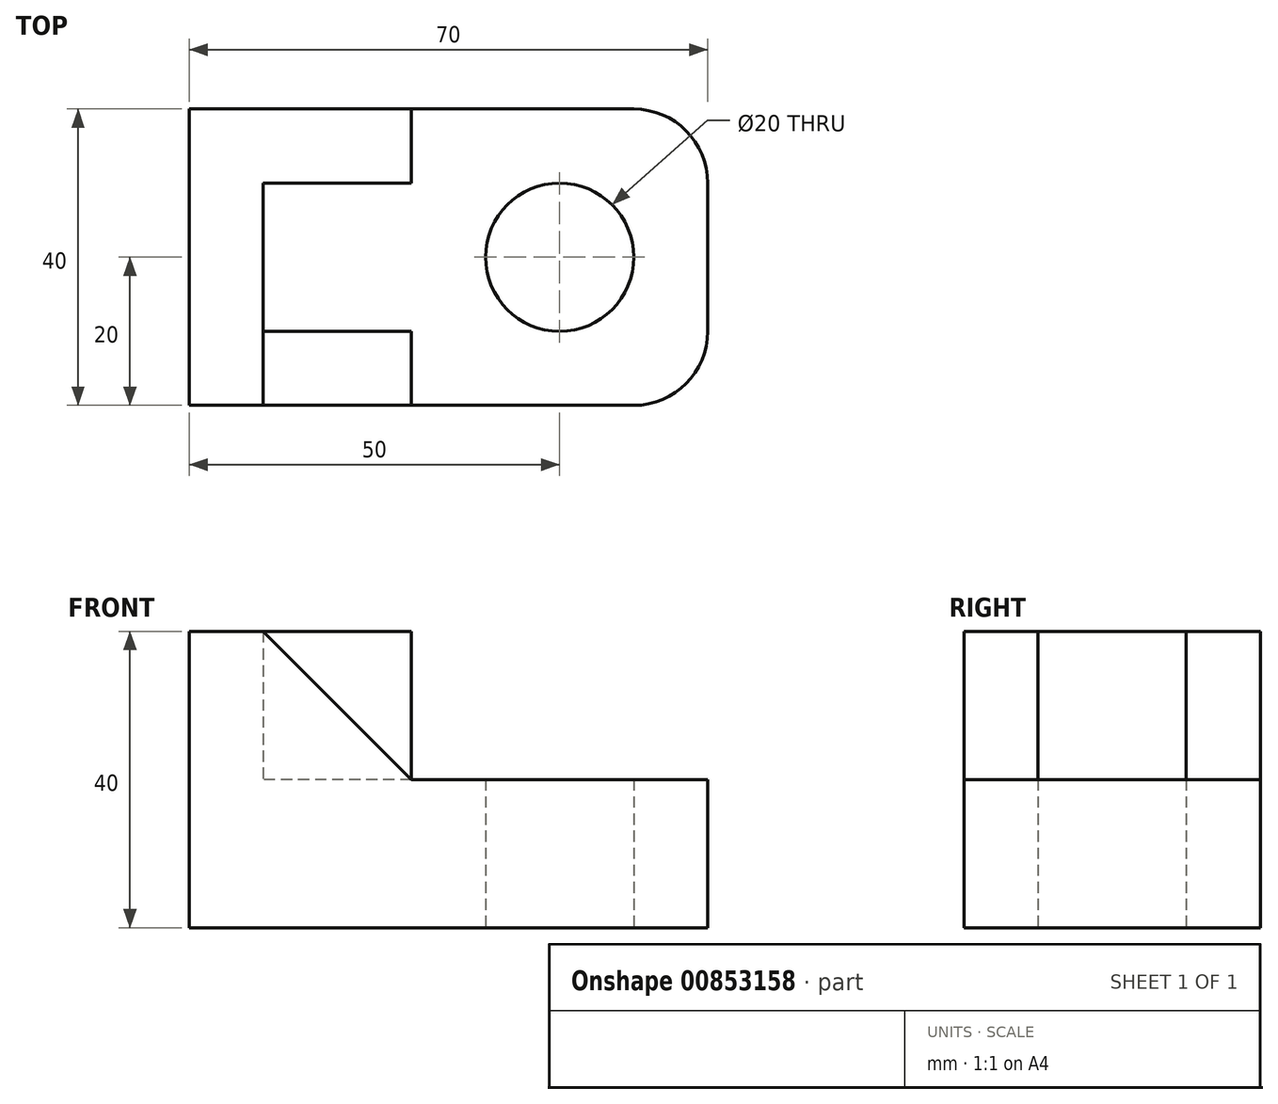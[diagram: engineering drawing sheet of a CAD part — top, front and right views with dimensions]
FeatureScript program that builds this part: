
annotation { "Feature Type Name" : "Feature", "Feature Type Description" : "" }
export const myFeature = defineFeature(function(context is Context, id is Id, definition is map)
    precondition{}
    {
        {
            var Q0;
            Q0=qCreatedBy(makeId("Top.planeOp"),FACE);
            var sketch = newSketch(context, id + "F0", { "sketchPlane" : qUnion([Q0])});
            skLineSegment(sketch, "E0.bottom", {"start": v(-35, -20) * mm, "end": v(25, -20) * mm});
            skLineSegment(sketch, "E0.top", {"start": v(-35, 20) * mm, "end": v(25, 20) * mm});
            skLineSegment(sketch, "E0.left", {"start": v(-35, -20) * mm, "end": v(-35, 20) * mm});
            skLineSegment(sketch, "E0.right", {"start": v(35, -10) * mm, "end": v(35, 10) * mm});
            skCircle(sketch, "E1", {"center": v(15, 0) * mm, "radius": 10 * mm});
            skPoint(sketch, "E2.visualSharp", {"position": v(35, 20) * mm});
            skArc(sketch, "E2.filletArc", {"start": v(35, 10) * mm, "mid": v(32.07, 17.07) * mm, "end": v(25, 20) * mm});
            skPoint(sketch, "E3.visualSharp", {"position": v(35, -20) * mm});
            skArc(sketch, "E3.filletArc", {"start": v(25, -20) * mm, "mid": v(32.07, -17.07) * mm, "end": v(35, -10) * mm});
            skSolve(sketch);
        }
        {
            var Q0;
            Q0=makeQuery(id+"F0.imprint","IMPRINT",FACE,{"disambiguationData":[TD([[makeQuery(id+"F0.imprint","IMPRINT",EDGE,{"derivedFrom":sQuery(id+"F0.wireOp",EDGE,"E0.bottom")}),1.0]])]});
            extrude(context, id + "F1", {"entities" : qUnion([Q0]), "depth" : 20 * mm, "offsetDistance" : 25 * mm});
        }
        {
            var Q0;
            Q0=makeQuery(id+"F1.opExtrude","CAP_FACE",FACE,{"disambiguationData":[OSD([sQuery(id+"F0.wireOp",EDGE,"E0.bottom"),sQuery(id+"F0.wireOp",EDGE,"E0.top"),sQuery(id+"F0.wireOp",EDGE,"E0.left"),sQuery(id+"F0.wireOp",EDGE,"E0.right"),sQuery(id+"F0.wireOp",EDGE,"E1"),sQuery(id+"F0.wireOp",EDGE,"E2.filletArc"),sQuery(id+"F0.wireOp",EDGE,"E3.filletArc")])],"isStart":false});
            var sketch = newSketch(context, id + "F2", { "sketchPlane" : qUnion([Q0])});
            skLineSegment(sketch, "E4", {"start": v(-35, 20) * mm, "end": v(-35, -20) * mm});
            skLineSegment(sketch, "E5", {"start": v(-35, -20) * mm, "end": v(-5, -20) * mm});
            skLineSegment(sketch, "E6", {"start": v(-5, -20) * mm, "end": v(-5, -10) * mm});
            skLineSegment(sketch, "E7", {"start": v(-5, -10) * mm, "end": v(-25, -10) * mm});
            skLineSegment(sketch, "E8", {"start": v(-25, -10) * mm, "end": v(-25, 10) * mm});
            skLineSegment(sketch, "E9", {"start": v(-25, 10) * mm, "end": v(-5, 10) * mm});
            skLineSegment(sketch, "E10", {"start": v(-5, 10) * mm, "end": v(-5, 20) * mm});
            skLineSegment(sketch, "E11", {"start": v(-5, 20) * mm, "end": v(-35, 20) * mm});
            skSolve(sketch);
        }
        {
            var Q0;
            Q0=makeQuery(id+"F2.imprint","IMPRINT",FACE,{"disambiguationData":[TD([[makeQuery(id+"F2.imprint","IMPRINT",EDGE,{"derivedFrom":sQuery(id+"F2.wireOp",EDGE,"E4")}),-1.0]])]});
            extrude(context, id + "F3", {"entities" : qUnion([Q0]), "operationType" : NewBodyOperationType.ADD, "depth" : 20 * mm, "offsetDistance" : 25 * mm});
        }
        {
            var Q0;
            Q0=makeQuery(id+"F3.boolean.opBoolean","MERGE",FACE,{"derivedFrom":[makeQuery(id+"F1.opExtrude","SWEPT_FACE",FACE,{"disambiguationData":[OSD([sQuery(id+"F0.wireOp",EDGE,"E0.bottom")])]}),makeQuery(id+"F3.opExtrude","SWEPT_FACE",FACE,{"disambiguationData":[OSD([sQuery(id+"F2.wireOp",EDGE,"E5")])]})]});
            var sketch = newSketch(context, id + "F4", { "sketchPlane" : qUnion([Q0])});
            skLineSegment(sketch, "E12", {"start": v(-5, 20) * mm, "end": v(-5, 40) * mm});
            skLineSegment(sketch, "E13", {"start": v(-5, 40) * mm, "end": v(-25, 40) * mm});
            skLineSegment(sketch, "E14", {"start": v(-25, 40) * mm, "end": v(-5, 20) * mm});
            skSolve(sketch);
        }
        {
            var Q0;
            Q0=makeQuery(id+"F4.imprint","IMPRINT",FACE,{"disambiguationData":[TD([[makeQuery(id+"F4.imprint","IMPRINT",EDGE,{"derivedFrom":sQuery(id+"F4.wireOp",EDGE,"E12")}),-1.0]])]});
            extrude(context, id + "F5", {"entities" : qUnion([Q0]), "operationType" : NewBodyOperationType.REMOVE, "endBound" : BoundingType.UP_TO_NEXT, "oppositeDirection" : true, "depth" : 25 * mm, "offsetDistance" : 25 * mm});
        }
    });
